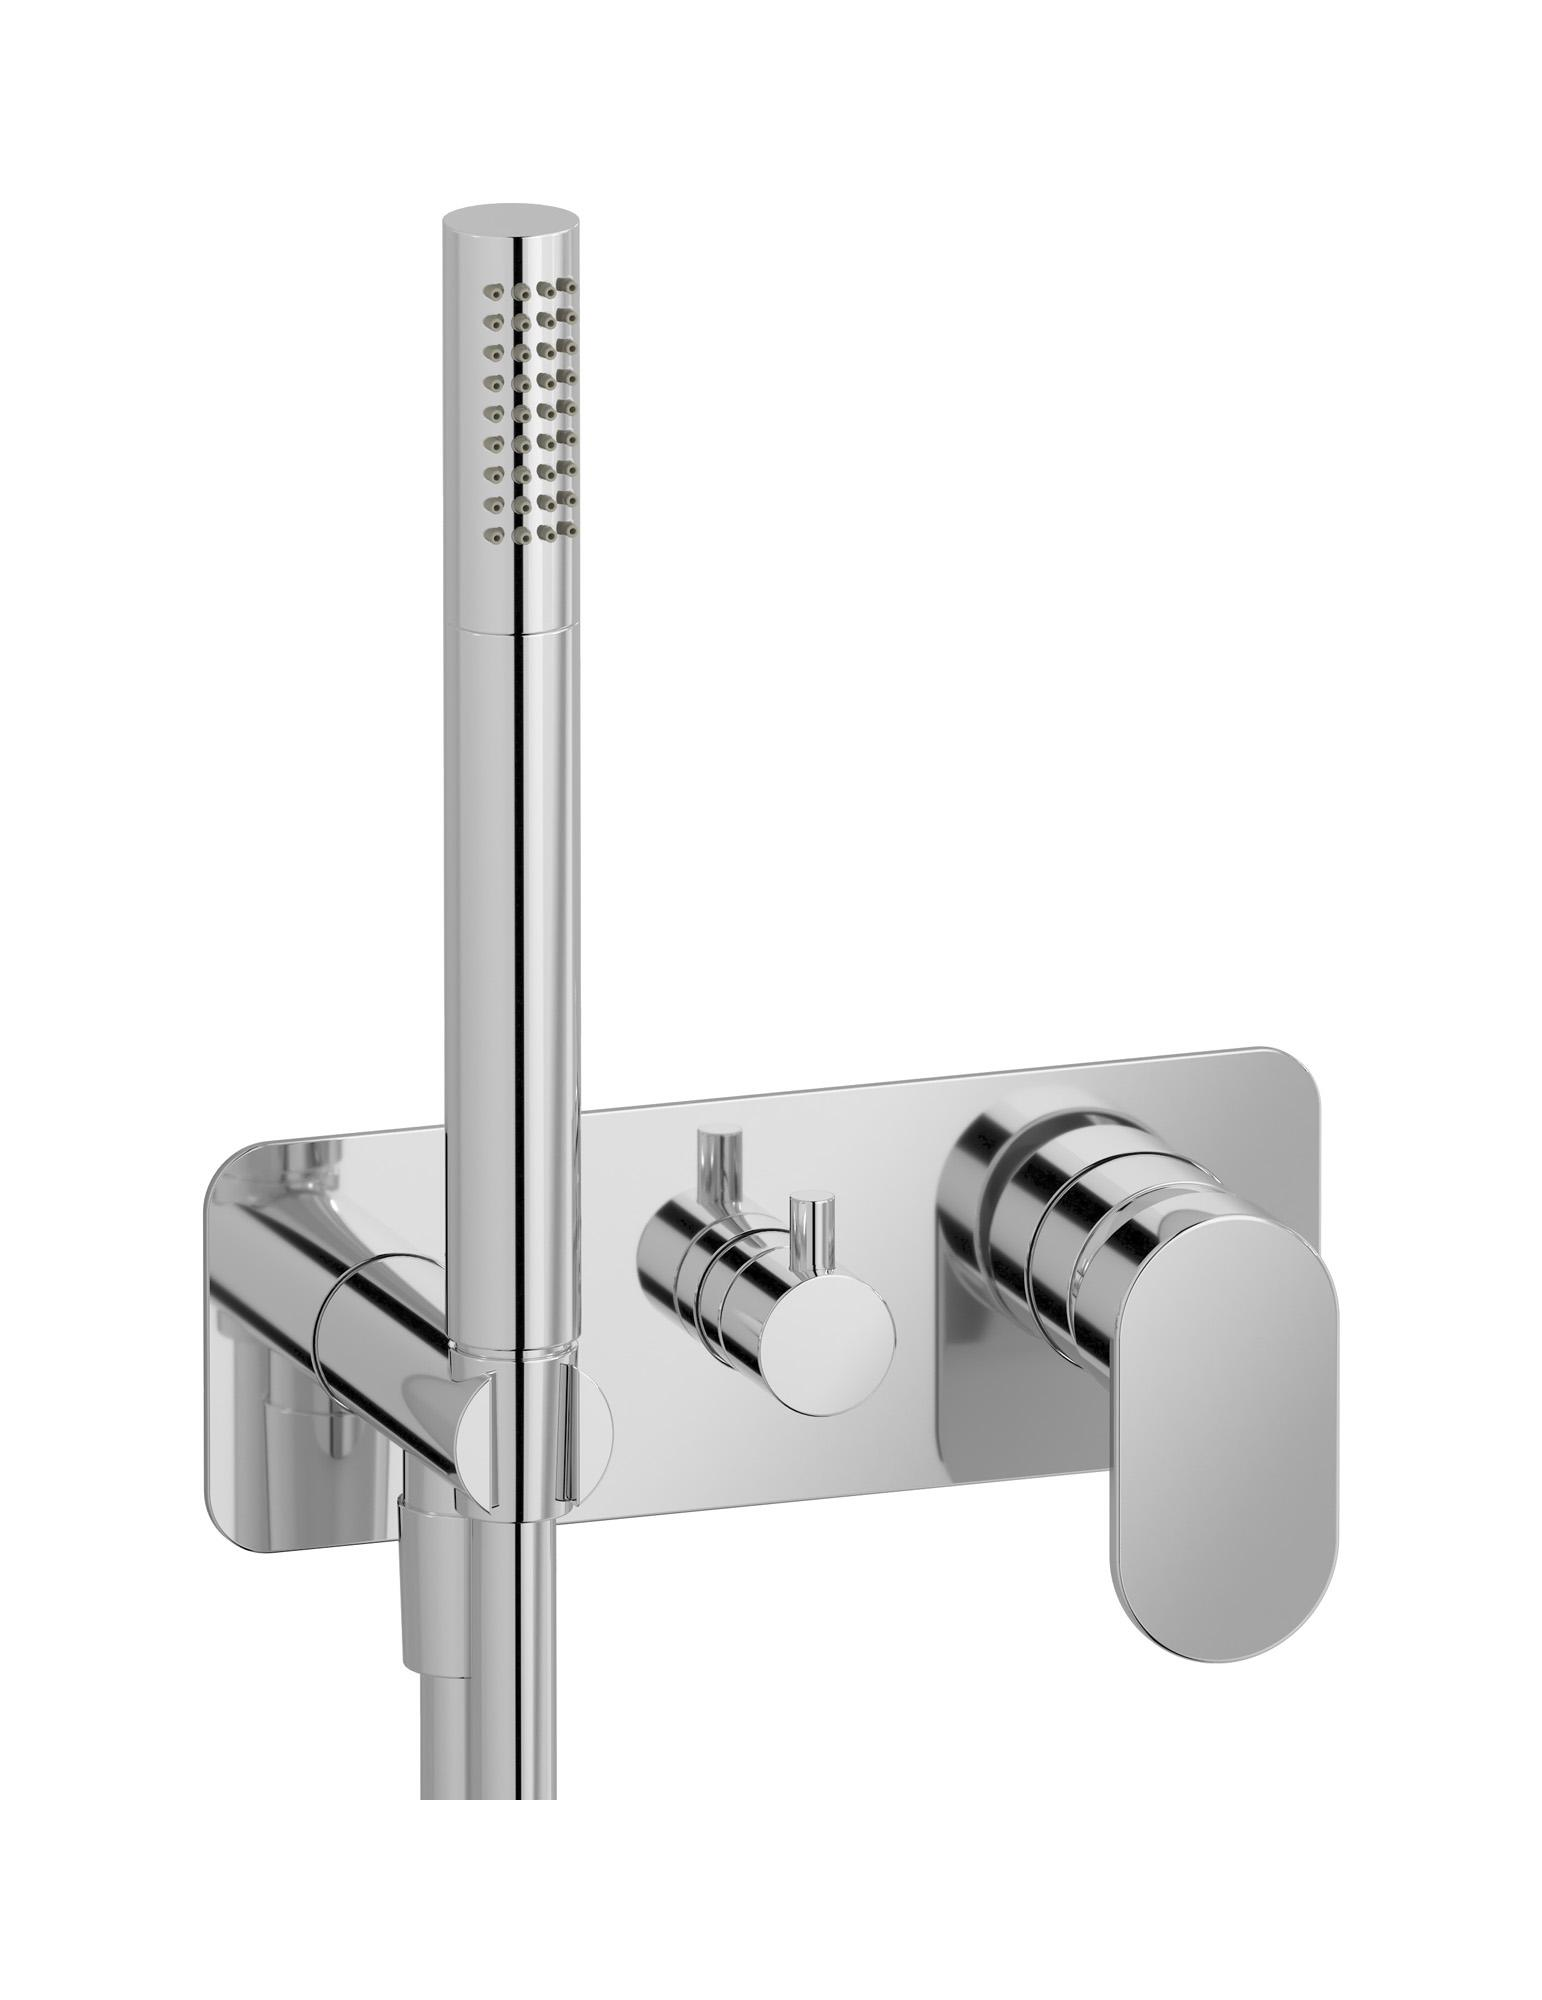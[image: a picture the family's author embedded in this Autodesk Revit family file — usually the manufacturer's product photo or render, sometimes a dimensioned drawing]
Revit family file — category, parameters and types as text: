
# Revit family: K2314
name_source: partatom
category: Apparecchi idraulici
units: mm (PartAtom-declared; Revit-internal decimal feet)

## family parameters
Basato su piano di lavoro = No
Condiviso = No
Mantieni orientamento annotazione = No
Numero OmniClass = 23.45.55.17
Punto di calcolo locali = No
Quota connettore circolare = Usa diametro
Sempre verticale = Sì
Taglio con vuoti quando caricato = No
Tipo di parte = Normale
Titolo OmniClass = Mixing Faucets

## types (9) — shared parameters
Cold water inlet = 10 mm  [stored 0.0328084 ft]
Commenti sul tipo = Wall mixer
Connessione CW = No
Connessione HW = No
Connessione di scarico = No
Connessione di ventilazione = No
Descrizione = Exposed parts for manual wall mixer with three ways diverter and shower kit
Hot water inlet = 10 mm  [stored 0.0328084 ft]
Produttore = IB Rubinetterie S.p.A.
URL = https://www.weareib.it
zero-valued in all types: Prospetto di default

## per-type parameters (varying)
| type | Finishes surface | Immagine tipo | Modello |
| Chrome | IB_Chrome | K2314CC.jpg | K2314CC |
| Brushed nickel | IB_Brushed nickel | K2314SS.jpg | K2314SS |
| Matt black | IB_matt black | K2314NP.jpg | K2314NP |
| Matt white | IB_matt white | K2314BO.jpg | K2314BO |
| Pale gold | IB_Pale gold | K2314II.jpg | K2314II |
| Brushed pale gold | IB_brushed pale gold | K2314IS.jpg | K2314IS |
| Rose gold | IB_brushed pale gold | K2314RS.jpg | K2314RS |
| Gold | IB_gold | K2314OO.jpg | K2314OO |
| Platinum | IB_Platinum | K2314PL.jpg | K2314PL |

note: [stored X ft] marks values corroborated as IEEE doubles in the binary element streams (Revit-internal decimal feet)
